# Revit family: 111010001042001
name_source: partatom
category: Perfiles
revit_build: Autodesk Revit 2018 (Build: 20190510_1515(x64)
units: mm (PartAtom-declared; Revit-internal decimal feet)

## family parameters
Forma de sección = Sin definir
Rotar con componente = No
Uso de perfil = Barrido de muro

## types (1)
- ESQUINERO ENCUENTRO PVC 10MM BLANCO TIRA 2.5MT
    Altura = 10 mm  [stored 0.0328084 ft]
    Aplicacion = En proyectos donde se utilice cerámica, para dar acabado y protección en las esquinas.
    Color = Blanco
    Descripción = Esquinero encuentro 10 MM
    Dimension = 10 mm  [stored 0.0328084 ft]
    Dureza = Shore D 80
    Empresa = CNP SPA.
    Espesor = 2 mm  [stored 0.00656168 ft]
    Largo = 2500 mm  [stored 8.2021 ft]
    Material = <Por categoría>
    Modelo = ESQUINERO ENCUENTRO PVC
    Nombre SKU = ESQUINERO ENCUENTRO PVC 10MM BLANCO TIRA 2.5MT
    Num SKUs = 111010001042001
    URL = https://www.empresascnp.cl
    Unidad = Tiras de 2,5 Metros.
    Url Ficha tecnica = https://empresascnp.cl
    Uso = Se utiliza como esquinero para la protección o decoración
de las esquinas de las cerámicas o planchas, en el revestimiento
de las obras constructivas.
    Ventajas = Autoextinguible

note: [stored X ft] marks values corroborated as IEEE doubles in the binary element streams (Revit-internal decimal feet)

## geometry (parser evidence)
native form markers: Blend x4
no freeform markers — native parametric forms only
